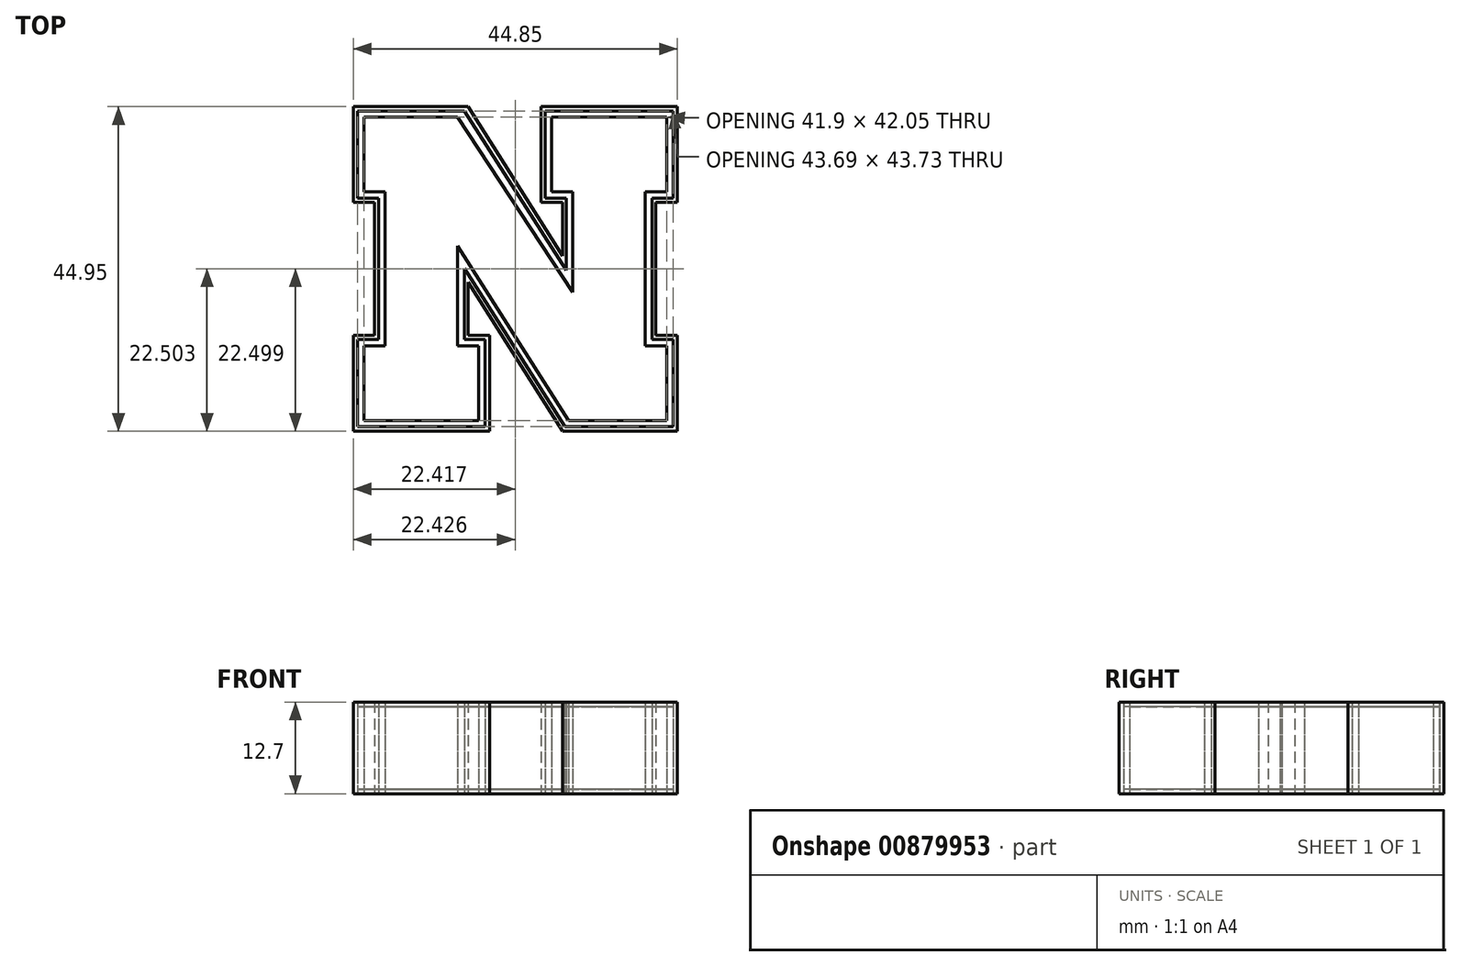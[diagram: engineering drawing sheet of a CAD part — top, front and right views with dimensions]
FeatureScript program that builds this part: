
annotation { "Feature Type Name" : "Feature", "Feature Type Description" : "" }
export const myFeature = defineFeature(function(context is Context, id is Id, definition is map)
    precondition{}
    {
        {
            var Q0;
            Q0=qCreatedBy(makeId("Top.planeOp"),FACE);
            var sketch = newSketch(context, id + "F0", { "sketchPlane" : qUnion([Q0])});
            skLineSegment(sketch, "E0", {"start": v(-59, 15.92) * mm, "end": v(-59, 2.65) * mm});
            skLineSegment(sketch, "E1", {"start": v(-59, 2.65) * mm, "end": v(-40.13, 2.65) * mm});
            skLineSegment(sketch, "E2", {"start": v(-40.13, 2.65) * mm, "end": v(-40.13, 15.92) * mm});
            skLineSegment(sketch, "E3", {"start": v(-40.13, 15.92) * mm, "end": v(-43.09, 15.92) * mm});
            skLineSegment(sketch, "E4", {"start": v(-43.09, 15.92) * mm, "end": v(-43.09, 23.3) * mm});
            skLineSegment(sketch, "E5", {"start": v(-43.09, 23.3) * mm, "end": v(-30, 2.65) * mm});
            skLineSegment(sketch, "E6", {"start": v(-30, 2.65) * mm, "end": v(-14.15, 2.65) * mm});
            skLineSegment(sketch, "E7", {"start": v(-14.15, 2.65) * mm, "end": v(-14.15, 15.92) * mm});
            skLineSegment(sketch, "E8", {"start": v(-14.15, 15.92) * mm, "end": v(-17.1, 15.92) * mm});
            skLineSegment(sketch, "E9", {"start": v(-17.1, 15.92) * mm, "end": v(-17.1, 34.32) * mm});
            skLineSegment(sketch, "E10", {"start": v(-17.1, 34.32) * mm, "end": v(-14.15, 34.32) * mm});
            skLineSegment(sketch, "E11", {"start": v(-14.15, 34.32) * mm, "end": v(-14.15, 47.6) * mm});
            skLineSegment(sketch, "E12", {"start": v(-14.15, 47.6) * mm, "end": v(-33.01, 47.6) * mm});
            skLineSegment(sketch, "E13", {"start": v(-33.01, 47.6) * mm, "end": v(-33.01, 34.32) * mm});
            skLineSegment(sketch, "E14", {"start": v(-33.01, 34.32) * mm, "end": v(-30, 34.32) * mm});
            skLineSegment(sketch, "E15", {"start": v(-30, 34.32) * mm, "end": v(-30, 26.95) * mm});
            skLineSegment(sketch, "E16", {"start": v(-30, 26.95) * mm, "end": v(-43.09, 47.6) * mm});
            skLineSegment(sketch, "E17", {"start": v(-43.09, 47.6) * mm, "end": v(-59, 47.6) * mm});
            skLineSegment(sketch, "E18", {"start": v(-59, 47.6) * mm, "end": v(-59, 34.32) * mm});
            skLineSegment(sketch, "E19", {"start": v(-59, 34.32) * mm, "end": v(-56.06, 34.32) * mm});
            skLineSegment(sketch, "E20", {"start": v(-56.06, 34.32) * mm, "end": v(-56.06, 15.92) * mm});
            skLineSegment(sketch, "E21", {"start": v(-56.06, 15.92) * mm, "end": v(-59, 15.92) * mm});
            skSolve(sketch);
        }
        {
            var Q0;
            Q0=makeQuery(id+"F0.imprint","IMPRINT",FACE,{"disambiguationData":[TD([[makeQuery(id+"F0.imprint","IMPRINT",EDGE,{"derivedFrom":sQuery(id+"F0.wireOp",EDGE,"E0")}),1.0]])]});
            var sketch = newSketch(context, id + "F1", { "sketchPlane" : qUnion([Q0])});
            skLineSegment(sketch, "E22", {"start": v(-58.43, 47) * mm, "end": v(-58.43, 34.92) * mm});
            skLineSegment(sketch, "E23", {"start": v(-58.43, 34.92) * mm, "end": v(-55.5, 34.92) * mm});
            skLineSegment(sketch, "E24", {"start": v(-55.5, 34.92) * mm, "end": v(-55.5, 15.38) * mm});
            skLineSegment(sketch, "E25", {"start": v(-55.5, 15.38) * mm, "end": v(-58.43, 15.38) * mm});
            skLineSegment(sketch, "E26", {"start": v(-58.43, 15.38) * mm, "end": v(-58.43, 3.28) * mm});
            skLineSegment(sketch, "E27", {"start": v(-58.43, 3.28) * mm, "end": v(-40.74, 3.28) * mm});
            skLineSegment(sketch, "E28", {"start": v(-40.74, 3.28) * mm, "end": v(-40.74, 15.38) * mm});
            skLineSegment(sketch, "E29", {"start": v(-40.74, 15.38) * mm, "end": v(-43.59, 15.38) * mm});
            skLineSegment(sketch, "E30", {"start": v(-43.59, 15.38) * mm, "end": v(-43.59, 25.18) * mm});
            skLineSegment(sketch, "E31", {"start": v(-43.59, 25.18) * mm, "end": v(-29.72, 3.28) * mm});
            skLineSegment(sketch, "E32", {"start": v(-29.72, 3.28) * mm, "end": v(-14.74, 3.28) * mm});
            skLineSegment(sketch, "E33", {"start": v(-14.74, 3.28) * mm, "end": v(-14.74, 15.38) * mm});
            skLineSegment(sketch, "E34", {"start": v(-14.74, 15.38) * mm, "end": v(-17.66, 15.38) * mm});
            skLineSegment(sketch, "E35", {"start": v(-17.66, 15.38) * mm, "end": v(-17.66, 34.92) * mm});
            skLineSegment(sketch, "E36", {"start": v(-17.66, 34.92) * mm, "end": v(-14.74, 34.92) * mm});
            skLineSegment(sketch, "E37", {"start": v(-14.74, 34.92) * mm, "end": v(-14.74, 47.01) * mm});
            skLineSegment(sketch, "E38", {"start": v(-14.74, 47.01) * mm, "end": v(-32.44, 47.01) * mm});
            skLineSegment(sketch, "E39", {"start": v(-32.44, 47.01) * mm, "end": v(-32.44, 34.92) * mm});
            skLineSegment(sketch, "E40", {"start": v(-32.44, 34.92) * mm, "end": v(-29.5, 34.92) * mm});
            skLineSegment(sketch, "E41", {"start": v(-29.5, 34.92) * mm, "end": v(-29.5, 24.96) * mm});
            skLineSegment(sketch, "E42", {"start": v(-29.5, 24.96) * mm, "end": v(-43.59, 47.01) * mm});
            skLineSegment(sketch, "E43", {"start": v(-43.59, 47.01) * mm, "end": v(-58.43, 47) * mm});
            skSolve(sketch);
        }
        {
            var Q0;
            Q0=makeQuery(id+"F1.imprint","IMPRINT",FACE,{"disambiguationData":[TD([[makeQuery(id+"F1.imprint","IMPRINT",EDGE,{"derivedFrom":sQuery(id+"F1.wireOp",EDGE,"E22")}),-1.0]])]});
            var sketch = newSketch(context, id + "F2", { "sketchPlane" : qUnion([Q0])});
            skLineSegment(sketch, "E44", {"start": v(-57.53, 46.13) * mm, "end": v(-57.53, 35.81) * mm});
            skLineSegment(sketch, "E45", {"start": v(-57.53, 35.81) * mm, "end": v(-54.6, 35.81) * mm});
            skLineSegment(sketch, "E46", {"start": v(-54.6, 35.81) * mm, "end": v(-54.6, 14.47) * mm});
            skLineSegment(sketch, "E47", {"start": v(-54.6, 14.47) * mm, "end": v(-57.53, 14.47) * mm});
            skLineSegment(sketch, "E48", {"start": v(-57.53, 14.47) * mm, "end": v(-57.53, 4.13) * mm});
            skLineSegment(sketch, "E49", {"start": v(-57.53, 4.13) * mm, "end": v(-41.64, 4.13) * mm});
            skLineSegment(sketch, "E50", {"start": v(-41.64, 4.13) * mm, "end": v(-41.64, 14.47) * mm});
            skLineSegment(sketch, "E51", {"start": v(-41.64, 14.47) * mm, "end": v(-44.54, 14.47) * mm});
            skLineSegment(sketch, "E52", {"start": v(-44.54, 14.47) * mm, "end": v(-44.54, 28.32) * mm});
            skLineSegment(sketch, "E53", {"start": v(-44.54, 28.32) * mm, "end": v(-29.2, 4.13) * mm});
            skLineSegment(sketch, "E54", {"start": v(-29.2, 4.13) * mm, "end": v(-15.62, 4.13) * mm});
            skLineSegment(sketch, "E55", {"start": v(-15.62, 4.13) * mm, "end": v(-15.62, 14.47) * mm});
            skLineSegment(sketch, "E56", {"start": v(-15.62, 14.47) * mm, "end": v(-18.58, 14.47) * mm});
            skLineSegment(sketch, "E57", {"start": v(-18.58, 14.47) * mm, "end": v(-18.58, 35.81) * mm});
            skLineSegment(sketch, "E58", {"start": v(-18.58, 35.81) * mm, "end": v(-15.62, 35.81) * mm});
            skLineSegment(sketch, "E59", {"start": v(-15.62, 35.81) * mm, "end": v(-15.62, 46.18) * mm});
            skLineSegment(sketch, "E60", {"start": v(-15.62, 46.18) * mm, "end": v(-31.54, 46.18) * mm});
            skLineSegment(sketch, "E61", {"start": v(-31.54, 46.18) * mm, "end": v(-31.54, 35.81) * mm});
            skLineSegment(sketch, "E62", {"start": v(-31.54, 35.81) * mm, "end": v(-28.63, 35.81) * mm});
            skLineSegment(sketch, "E63", {"start": v(-28.63, 35.81) * mm, "end": v(-28.63, 21.92) * mm});
            skLineSegment(sketch, "E64", {"start": v(-28.63, 21.92) * mm, "end": v(-44.54, 46.18) * mm});
            skLineSegment(sketch, "E65", {"start": v(-44.54, 46.18) * mm, "end": v(-57.53, 46.13) * mm});
            skSolve(sketch);
        }
        {
            var Q0;
            Q0=makeQuery(id+"F2.imprint","IMPRINT",FACE,{"disambiguationData":[TD([[makeQuery(id+"F2.imprint","IMPRINT",EDGE,{"derivedFrom":sQuery(id+"F2.wireOp",EDGE,"E44")}),1.0]])]});
            var Q1;
            Q1=makeQuery(id+"F1.imprint","IMPRINT",FACE,{"disambiguationData":[TD([[makeQuery(id+"F1.imprint","IMPRINT",EDGE,{"derivedFrom":sQuery(id+"F1.wireOp",EDGE,"E22")}),-1.0]])]});
            extrude(context, id + "F3", {"entities" : qUnion([Q0, Q1]), "endBound" : BoundingType.SYMMETRIC, "depth" : 12.7 * mm, "offsetDistance" : 25.4 * mm});
        }
        {
            var Q0;
            Q0=makeQuery(id+"F2.imprint","IMPRINT",FACE,{"disambiguationData":[TD([[makeQuery(id+"F2.imprint","IMPRINT",EDGE,{"derivedFrom":sQuery(id+"F2.wireOp",EDGE,"E44")}),-1.0]])]});
            extrude(context, id + "F4", {"entities" : qUnion([Q0]), "endBound" : BoundingType.SYMMETRIC, "depth" : 11.43 * mm, "offsetDistance" : 25.4 * mm});
        }
    });
